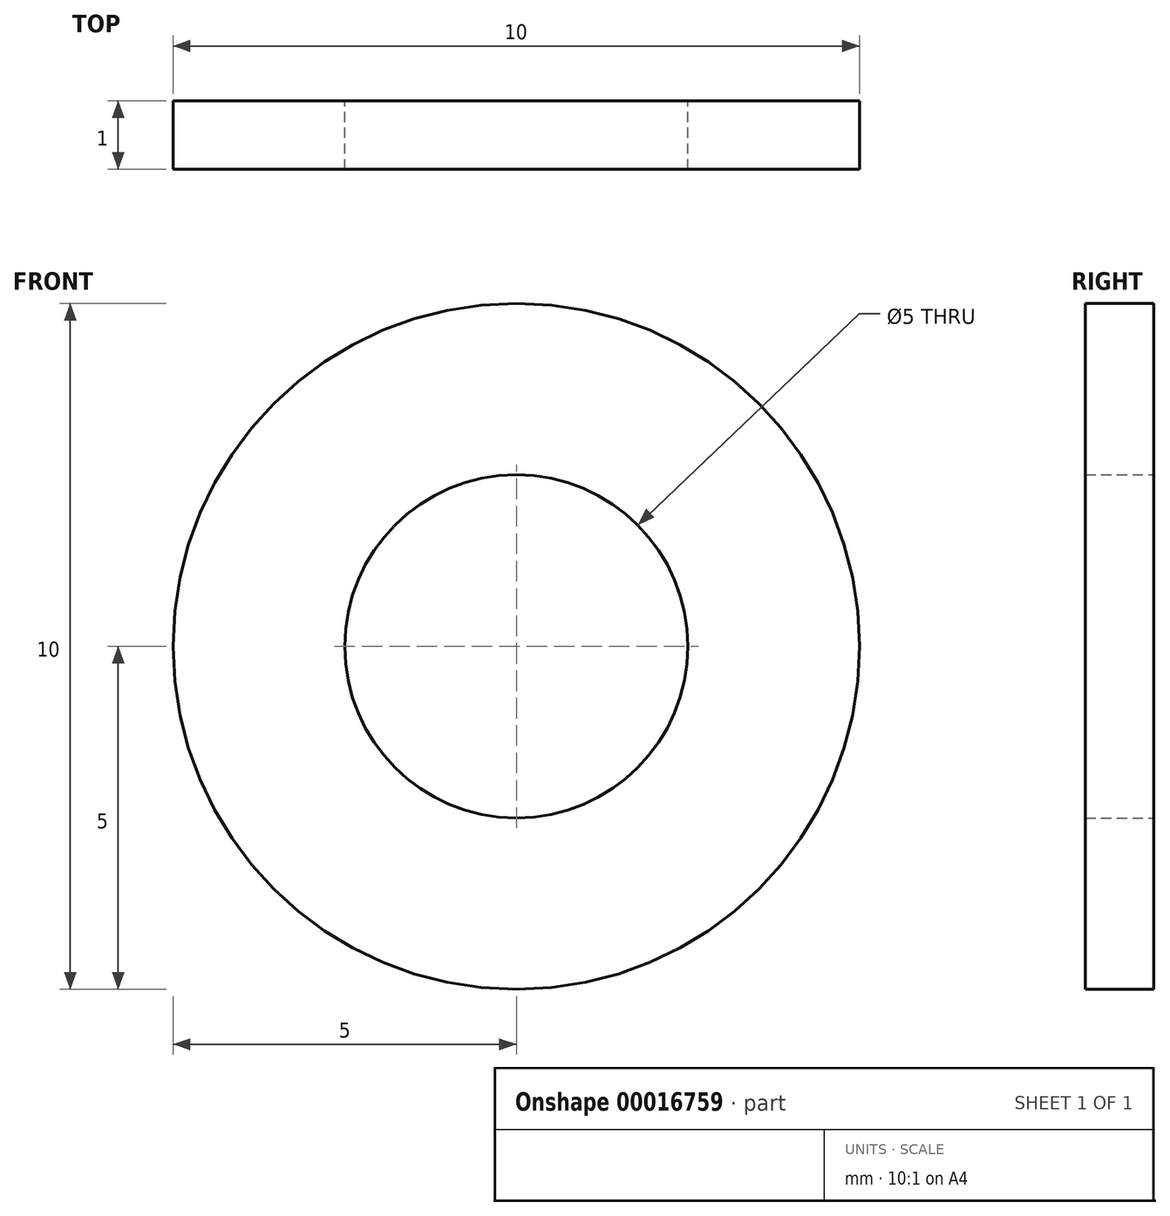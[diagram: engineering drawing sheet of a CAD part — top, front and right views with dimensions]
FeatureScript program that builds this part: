
annotation { "Feature Type Name" : "Feature", "Feature Type Description" : "" }
export const myFeature = defineFeature(function(context is Context, id is Id, definition is map)
    precondition{}
    {
        {
            var Q0;
            Q0=qCreatedBy(makeId("Front.planeOp"),FACE);
            var sketch = newSketch(context, id + "F0", { "sketchPlane" : qUnion([Q0])});
            skCircle(sketch, "E0", {"center": v(0, 0) * mm, "radius": 2.5 * mm});
            skCircle(sketch, "E1", {"center": v(0, 0) * mm, "radius": 5 * mm});
            skSolve(sketch);
        }
        {
            var Q0;
            Q0=makeQuery(id+"F0.imprint","IMPRINT",FACE,{"disambiguationData":[TD([[makeQuery(id+"F0.imprint","IMPRINT",EDGE,{"derivedFrom":sQuery(id+"F0.wireOp",EDGE,"E0")}),-1.0]])]});
            extrude(context, id + "F1", {"entities" : qUnion([Q0]), "endBound" : BoundingType.SYMMETRIC, "depth" : 1 * mm});
        }
    });
